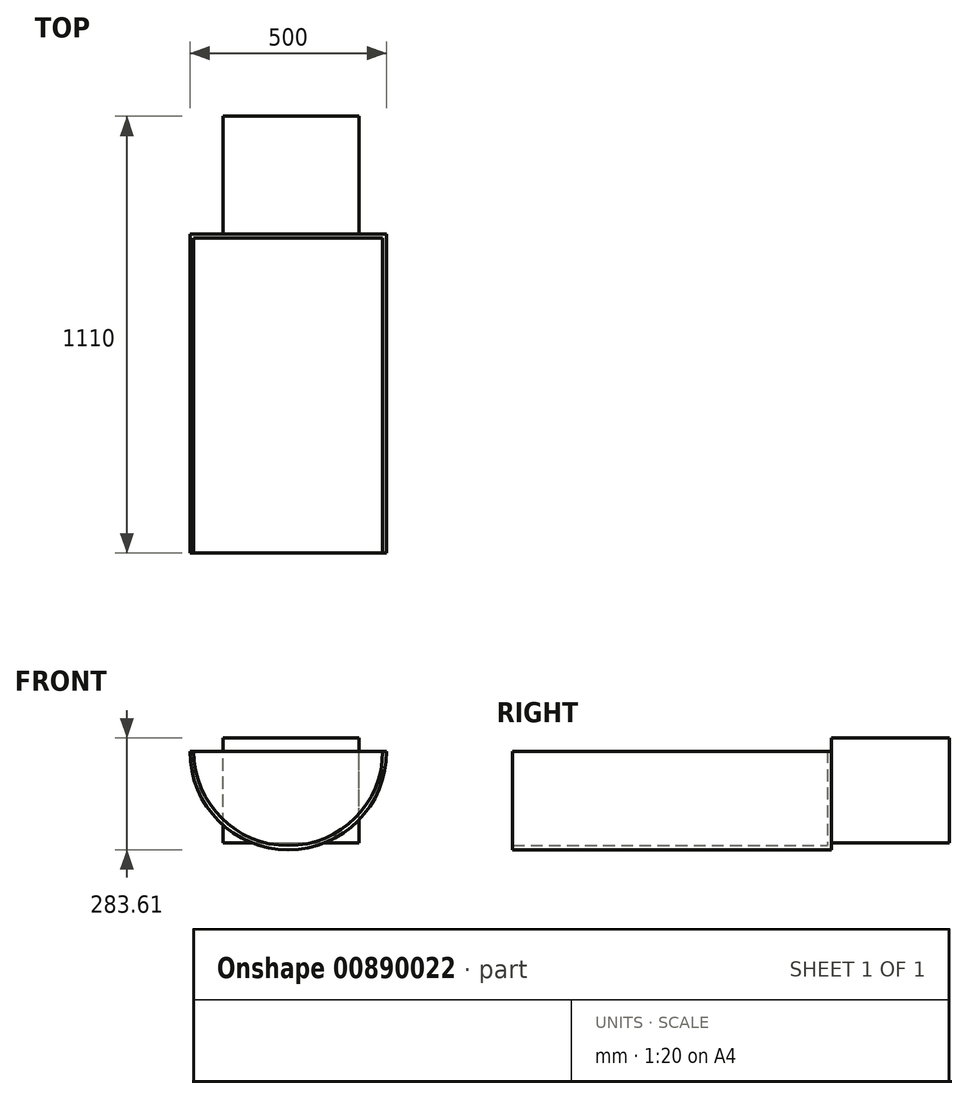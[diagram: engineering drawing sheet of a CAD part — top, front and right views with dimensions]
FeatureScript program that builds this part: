
annotation { "Feature Type Name" : "Feature", "Feature Type Description" : "" }
export const myFeature = defineFeature(function(context is Context, id is Id, definition is map)
    precondition{}
    {
        {
            var Q0;
            Q0=qCreatedBy(makeId("Front.planeOp"),FACE);
            var sketch = newSketch(context, id + "F0", { "sketchPlane" : qUnion([Q0])});
            skLineSegment(sketch, "E0", {"start": v(0, 0) * mm, "end": v(-500, 0) * mm});
            skArc(sketch, "E1", {"start": v(-500, 0) * mm, "mid": v(-250, -250) * mm, "end": v(0, 0) * mm});
            skLineSegment(sketch, "E2", {"start": v(0, 0) * mm, "end": v(-10, 0) * mm});
            skLineSegment(sketch, "E3", {"start": v(-500, 0) * mm, "end": v(-490, 0) * mm});
            skArc(sketch, "E4", {"start": v(-490, 0) * mm, "mid": v(-250, -239.69) * mm, "end": v(-10, 0) * mm});
            skSolve(sketch);
        }
        {
            var Q0;
            Q0=makeQuery(id+"F0.imprint","IMPRINT",FACE,{"disambiguationData":[TD([[makeQuery(id+"F0.imprint","IMPRINT",EDGE,{"derivedFrom":sQuery(id+"F0.wireOp",EDGE,"E1")}),1.0]])]});
            var Q1;
            Q1=makeQuery(id+"F0.imprint","IMPRINT",FACE,{"disambiguationData":[TD([[makeQuery(id+"F0.imprint","IMPRINT",EDGE,{"derivedFrom":sQuery(id+"F0.wireOp",EDGE,"E0")}),1.0]])]});
            extrude(context, id + "F1", {"entities" : qUnion([Q0, Q1]), "depth" : 10 * mm, "offsetDistance" : 25 * mm});
        }
        {
            var Q0;
            Q0=makeQuery(id+"F0.imprint","IMPRINT",FACE,{"disambiguationData":[TD([[makeQuery(id+"F0.imprint","IMPRINT",EDGE,{"derivedFrom":sQuery(id+"F0.wireOp",EDGE,"E1")}),1.0]])]});
            extrude(context, id + "F2", {"entities" : qUnion([Q0]), "operationType" : NewBodyOperationType.ADD, "oppositeDirection" : true, "depth" : 800 * mm, "offsetDistance" : 25 * mm});
        }
        {
            var Q0;
            Q0=makeQuery(id+"F2.opExtrude","CAP_FACE",FACE,{"disambiguationData":[OSD([sQuery(id+"F0.wireOp",EDGE,"E1"),sQuery(id+"F0.wireOp",EDGE,"E2"),sQuery(id+"F0.wireOp",EDGE,"E3"),sQuery(id+"F0.wireOp",EDGE,"E4")])],"isStart":false});
            var sketch = newSketch(context, id + "F3", { "sketchPlane" : qUnion([Q0])});
            skArc(sketch, "E5", {"start": v(0, 0) * mm, "mid": v(250, -250) * mm, "end": v(500, 0) * mm});
            skLineSegment(sketch, "E6", {"start": v(0, 0) * mm, "end": v(500, 0) * mm});
            skSolve(sketch);
        }
        {
            var Q0;
            {var subQ1=makeQuery(id+"F2.opExtrude","CAP_EDGE",EDGE,{"disambiguationData":[OSD([sQuery(id+"F0.wireOp",EDGE,"E4")])],"isStart":false});Q0=makeQuery(id+"F3.imprint","IMPRINT",FACE,{"disambiguationData":[TD([[makeQuery(id+"F3.imprint","IMPRINT",EDGE,{"derivedFrom":subQ1}),-1.0]])]});}
            extrude(context, id + "F4", {"entities" : qUnion([Q0]), "operationType" : NewBodyOperationType.ADD, "oppositeDirection" : true, "depth" : 10 * mm, "offsetDistance" : 25 * mm});
        }
        {
            var Q0;
            {var subQ0=sQuery(id+"F0.wireOp",EDGE,"E4");Q0=makeQuery(id+"F4.boolean.opBoolean","MERGE",FACE,{"derivedFrom":[makeQuery(id+"F2.opExtrude","CAP_FACE",FACE,{"disambiguationData":[OSD([sQuery(id+"F0.wireOp",EDGE,"E1"),sQuery(id+"F0.wireOp",EDGE,"E2"),sQuery(id+"F0.wireOp",EDGE,"E3"),subQ0])],"isStart":false}),makeQuery(id+"F4.opExtrude","CAP_FACE",FACE,{"disambiguationData":[OSD([subQ0,sQuery(id+"F3.wireOp",EDGE,"E6")])],"isStart":true})]});}
            var sketch = newSketch(context, id + "F5", { "sketchPlane" : qUnion([Q0])});
            skLineSegment(sketch, "E7.bottom", {"start": v(415.26, -232.13) * mm, "end": v(69.8, -232.13) * mm});
            skLineSegment(sketch, "E7.top", {"start": v(415.26, 33.61) * mm, "end": v(69.8, 33.61) * mm});
            skLineSegment(sketch, "E7.left", {"start": v(415.26, -232.13) * mm, "end": v(415.26, 33.61) * mm});
            skLineSegment(sketch, "E7.right", {"start": v(69.8, -232.13) * mm, "end": v(69.8, 33.61) * mm});
            skPoint(sketch, "E7.middle", {"position": v(242.53, -99.26) * mm});
            skSolve(sketch);
        }
        {
            var Q0;
            Q0 = qSketchRegion(id + "F5", true);
            extrude(context, id + "F6", {"entities" : qUnion([Q0]), "operationType" : NewBodyOperationType.ADD, "depth" : 300 * mm, "offsetDistance" : 25 * mm});
        }
    });
